# Revit family: ARCTIC PCSMC
name_source: partatom
category: Осветительные приборы
revit_build: Autodesk Revit 2016 (Build: 20161004_0715(x64)
units: mm (PartAtom-declared; Revit-internal decimal feet)

## family parameters
Источник света = Нет
Общий = Нет
Основа = Грань
При загрузке вырезать с полостями = Нет
Размер круглого соединителя = Использовать диаметр
Тип детали = Нормальный
Точка расчета площади = Нет

## types (1)
- ARCTIC PCSMC
    ADSK_Единица измерения = Шт.
    ADSK_Завод-изготовитель = ООО МГК Световые технологии
    ADSK_Классификация нагрузок = Прочее
    ADSK_Код изделия = 1069000030
    ADSK_Количество фаз = 1
    ADSK_Количество фаз числовое = 1
    ADSK_Коэффициент мощности = 0.96
    ADSK_Масса = 1.8
    ADSK_Наименование = Серия светильников для освещения небольших производственных цехов, паркингов, технических помещений. Светильники комплектуются рассеивателем, устойчивым к воздействию аммиака. Возможно изготовление светильников различных модификаций: со II классом защиты от поражения электрическим током, с аварийным блоком и управлением освещением. В роли источника света применяются люминисцентные лампы
    ADSK_Напряжение = 230 В
    ADSK_Номинальная мощность = 0 кВт
    ADSK_Полная мощность = 0 кВ·А
    ADSK_Размер_Высота = 110 мм
    ADSK_Размер_Длина = 670 мм
    ADSK_Размер_Ширина = 86 мм
    ADSK_Ток = 0 А
    ADSK_Энергоэффективность = 53 лм/Вт
    IP Class = IP65
    URL = https://ltcompany.com
    Блок аварийного питания = Нет
    Выбор ИС = IES ARCTIC PCSMC : ARCTIC 118 (PC/SMC) HF
    Группа модели = Светильники
    Изготовитель = ООО МГК Световые технологии
    Класс Защиты = I
    Класс пожароопасности = П-II,IIа
    Климатическая зона = УХЛ2
    Код по классификатору = D5020200
    Корпус = Корпус белый пластик
    Крепление = 5 мм
    Крепления.ширина = 440 мм
    Область использования = Магазины/бутики, Объекты бытового обслуживания, Промышленные предприятия, Складские объекты, Транспортные узлы (вокзалы, аэропорты)
    Описание = Серия светильников для освещения небольших производственных цехов, паркингов, технических помещений. Светильники комплектуются рассеивателем, устойчивым к воздействию аммиака. Возможно изготовление светильников различных модификаций: со II классом защиты от поражения электрическим током, с аварийным блоком и управлением освещением. В роли источника света применяются люминисцентные лампы
    Отметка по умолчанию = 0 мм
    Плафон = Плафон самосвечение
    Полная установленная мощность = 0 кВ·А
    Тип ИС = ЛЛ
    Тип ПРА = ЭПРА
    Тип продукции = Светильник
